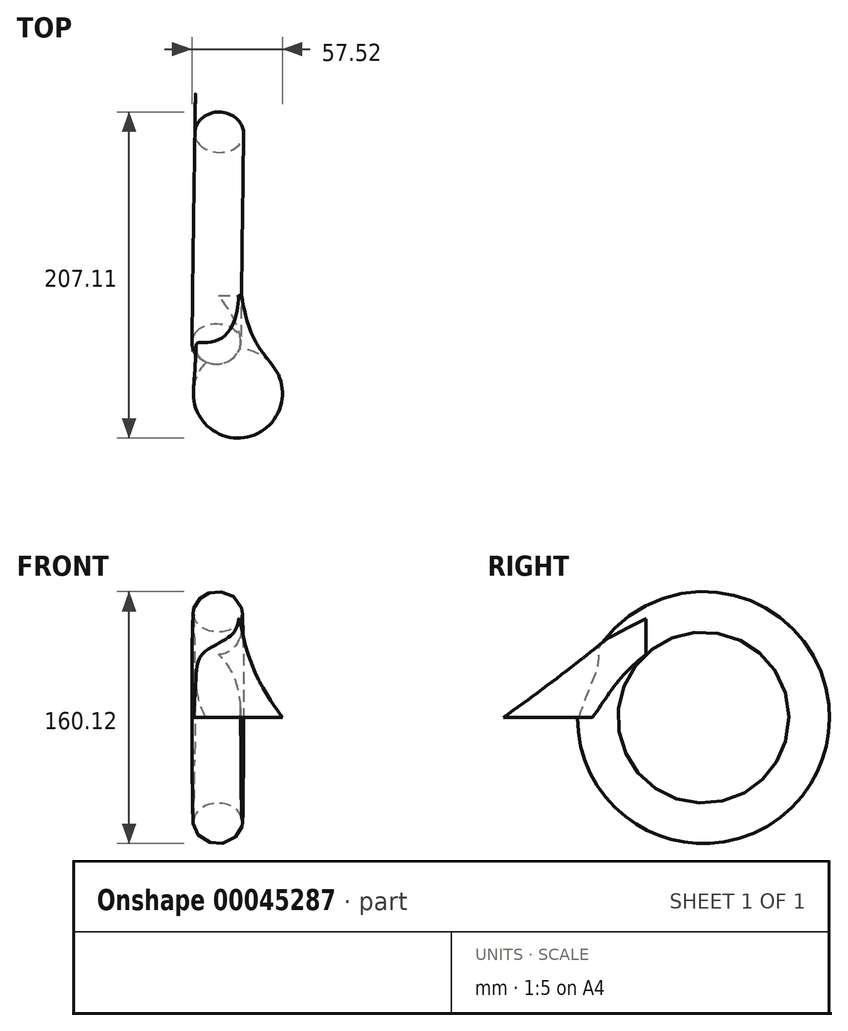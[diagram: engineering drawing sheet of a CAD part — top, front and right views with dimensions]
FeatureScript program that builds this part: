
annotation { "Feature Type Name" : "Feature", "Feature Type Description" : "" }
export const myFeature = defineFeature(function(context is Context, id is Id, definition is map)
    precondition{}
    {
        {
            var Q0;
            Q0=qCreatedBy(makeId("Top.planeOp"),FACE);
            var sketch = newSketch(context, id + "F0", { "sketchPlane" : qUnion([Q0])});
            skCircle(sketch, "E0", {"center": v(13.28, -62.12) * mm, "radius": 28.32 * mm});
            skSolve(sketch);
        }
        {
            var Q0;
            Q0=qCreatedBy(makeId("Front.planeOp"),FACE);
            var sketch = newSketch(context, id + "F1", { "sketchPlane" : qUnion([Q0])});
            skCircle(sketch, "E1", {"center": v(0, 55.7) * mm, "radius": 15.5 * mm});
            skSolve(sketch);
        }
        {
            var Q0;
            Q0=makeQuery(id+"F0.imprint","IMPRINT",FACE,{"disambiguationData":[TD([[makeQuery(id+"F0.imprint","IMPRINT",EDGE,{"derivedFrom":sQuery(id+"F0.wireOp",EDGE,"E0")}),1.0]])]});
            var Q1;
            Q1=makeQuery(id+"F1.imprint","IMPRINT",FACE,{"disambiguationData":[TD([[makeQuery(id+"F1.imprint","IMPRINT",EDGE,{"derivedFrom":sQuery(id+"F1.wireOp",EDGE,"E1")}),1.0]])]});
            loft(context, id + "F2", {"sheetProfilesArray" : [{ "sheetProfileEntities" : qUnion([Q0]) }, { "sheetProfileEntities" : qUnion([Q1]) }]});
        }
        {
            var Q0;
            Q0=qCreatedBy(makeId("Top.planeOp"),FACE);
            var sketch = newSketch(context, id + "F3", { "sketchPlane" : qUnion([Q0])});
            skLineSegment(sketch, "E2", {"start": v(-114.3, 38.2) * mm, "end": v(118.49, 34.98) * mm});
            skSolve(sketch);
        }
        {
            var Q0;
            Q0=makeQuery(id+"F2.opLoft","CAP_FACE",FACE,{"disambiguationData":[OSD([makeQuery(id+"F1.imprint","IMPRINT",FACE,{"disambiguationData":[TD([[makeQuery(id+"F1.imprint","IMPRINT",EDGE,{"derivedFrom":sQuery(id+"F1.wireOp",EDGE,"E1")}),1.0]])]})])],"isStart":true});
            var Q1;
            Q1=sQuery(id+"F3.wireOp",EDGE,"E2");
            revolve(context, id + "F4", {"operationType" : NewBodyOperationType.ADD, "entities" : qUnion([Q0]), "axis" : qUnion([Q1]), "revolveType" : RevolveType.FULL});
        }
    });
